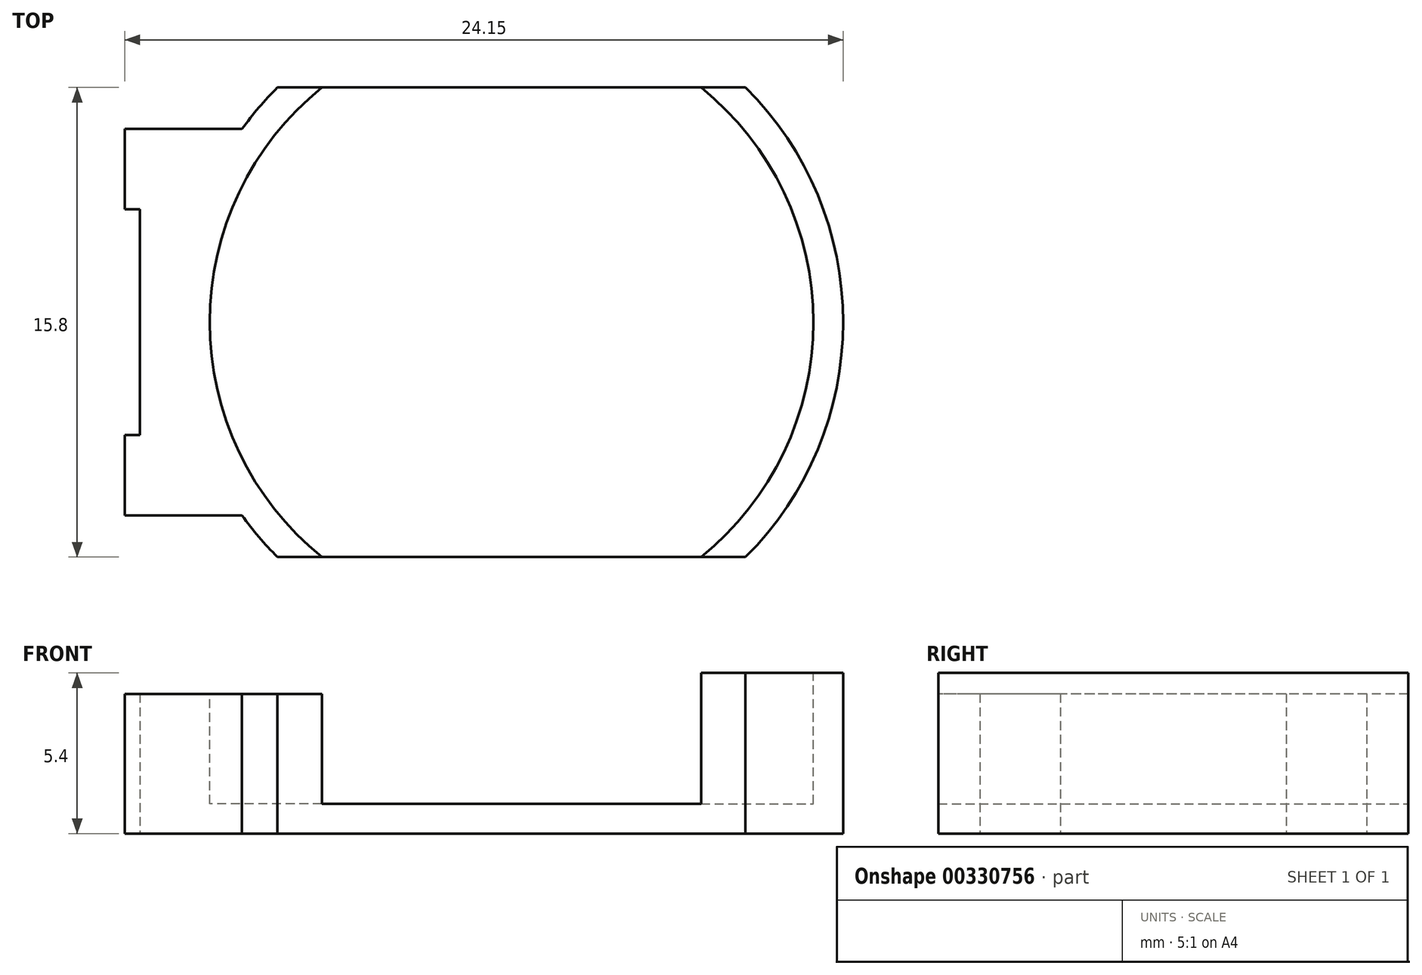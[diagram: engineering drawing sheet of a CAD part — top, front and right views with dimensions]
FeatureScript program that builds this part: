
annotation { "Feature Type Name" : "Feature", "Feature Type Description" : "" }
export const myFeature = defineFeature(function(context is Context, id is Id, definition is map)
    precondition{}
    {
        {
            var Q0;
            Q0=qCreatedBy(makeId("Top.planeOp"),FACE);
            var sketch = newSketch(context, id + "F0", { "sketchPlane" : qUnion([Q0])});
            skArc(sketch, "E0", {"start": v(-9.06, -6.5) * mm, "mid": v(-8.5, -7.22) * mm, "end": v(-7.87, -7.9) * mm});
            skLineSegment(sketch, "E1.bottom", {"start": v(-9.06, 6.5) * mm, "end": v(-13, 6.5) * mm});
            skLineSegment(sketch, "E1.top", {"start": v(-9.06, -6.5) * mm, "end": v(-13, -6.5) * mm});
            skLineSegment(sketch, "E1.right", {"start": v(-13, 6.5) * mm, "end": v(-13, 3.8) * mm});
            skLineSegment(sketch, "E2", {"start": v(-7.87, 7.9) * mm, "end": v(7.87, 7.9) * mm});
            skLineSegment(sketch, "E3", {"start": v(-7.87, -7.9) * mm, "end": v(7.87, -7.9) * mm});
            skArc(sketch, "E4.trimOffspring", {"start": v(-7.87, 7.9) * mm, "mid": v(-8.5, 7.22) * mm, "end": v(-9.06, 6.5) * mm});
            skArc(sketch, "E5.trimOffspring", {"start": v(7.87, -7.9) * mm, "mid": v(11.15, 0) * mm, "end": v(7.87, 7.9) * mm});
            skLineSegment(sketch, "E6.bottom", {"start": v(-13, 3.8) * mm, "end": v(-12.5, 3.8) * mm});
            skLineSegment(sketch, "E6.top", {"start": v(-13, -3.8) * mm, "end": v(-12.5, -3.8) * mm});
            skLineSegment(sketch, "E6.right", {"start": v(-12.5, 3.8) * mm, "end": v(-12.5, -3.8) * mm});
            skLineSegment(sketch, "E7.trimOffspring", {"start": v(-13, -3.8) * mm, "end": v(-13, -6.5) * mm});
            skSolve(sketch);
        }
        {
            var Q0;
            Q0=makeQuery(id+"F0.imprint","IMPRINT",FACE,{"disambiguationData":[TD([[makeQuery(id+"F0.imprint","IMPRINT",EDGE,{"derivedFrom":sQuery(id+"F0.wireOp",EDGE,"E0")}),1.0]])]});
            extrude(context, id + "F1", {"entities" : qUnion([Q0]), "depth" : 5.4 * mm});
        }
        {
            var Q0;
            Q0=makeQuery(id+"F1.opExtrude","CAP_FACE",FACE,{"disambiguationData":[OSD([sQuery(id+"F0.wireOp",EDGE,"E0"),sQuery(id+"F0.wireOp",EDGE,"E1.bottom"),sQuery(id+"F0.wireOp",EDGE,"E1.top"),sQuery(id+"F0.wireOp",EDGE,"E1.right"),sQuery(id+"F0.wireOp",EDGE,"E2"),sQuery(id+"F0.wireOp",EDGE,"E3"),sQuery(id+"F0.wireOp",EDGE,"E4.trimOffspring"),sQuery(id+"F0.wireOp",EDGE,"E5.trimOffspring"),sQuery(id+"F0.wireOp",EDGE,"E6.bottom"),sQuery(id+"F0.wireOp",EDGE,"E6.top"),sQuery(id+"F0.wireOp",EDGE,"E6.right"),sQuery(id+"F0.wireOp",EDGE,"E7.trimOffspring")])],"isStart":false});
            var sketch = newSketch(context, id + "F2", { "sketchPlane" : qUnion([Q0])});
            skCircle(sketch, "E8", {"center": v(0, 0) * mm, "radius": 10.15 * mm});
            skSolve(sketch);
        }
        {
            var Q0;
            {var subQ0=sQuery(id+"F2.wireOp",EDGE,"E8");var subQ1=makeQuery(id+"F1.opExtrude","CAP_EDGE",EDGE,{"disambiguationData":[OSD([sQuery(id+"F0.wireOp",EDGE,"E2")])],"isStart":false});var subQ2=makeQuery(id+"F2.imprint","INTERSECT",VERTEX,{"disambiguationData":[OD(0.0)],"derivedFrom":[subQ1,subQ0]});Q0=makeQuery(id+"F2.imprint","IMPRINT",FACE,{"disambiguationData":[TD([[makeQuery(id+"F2.imprint","IMPRINT",EDGE,{"disambiguationData":[TD([[subQ2,-1.0]])],"derivedFrom":subQ0}),1.0]])]});}
            extrude(context, id + "F3", {"entities" : qUnion([Q0]), "operationType" : NewBodyOperationType.REMOVE, "oppositeDirection" : true, "depth" : (5.4 - 1) * mm});
        }
        {
            var Q0;
            {var subQ0=sQuery(id+"F0.wireOp",EDGE,"E6.right");var subQ1=sQuery(id+"F0.wireOp",EDGE,"E6.bottom");var subQ2=sQuery(id+"F0.wireOp",EDGE,"E4.trimOffspring");var subQ3=sQuery(id+"F0.wireOp",EDGE,"E3");var subQ4=sQuery(id+"F0.wireOp",EDGE,"E2");var subQ5=sQuery(id+"F0.wireOp",EDGE,"E6.top");var subQ6=sQuery(id+"F0.wireOp",EDGE,"E0");var subQ7=sQuery(id+"F0.wireOp",EDGE,"E1.right");var subQ8=sQuery(id+"F0.wireOp",EDGE,"E1.bottom");var subQ9=sQuery(id+"F0.wireOp",EDGE,"E1.top");var subQ11=sQuery(id+"F0.wireOp",EDGE,"E7.trimOffspring");Q0=makeQuery(id+"F3.boolean.opBoolean","SPLIT",FACE,{"disambiguationData":[TD([makeQuery(id+"F1.opExtrude","SWEPT_FACE",FACE,{"disambiguationData":[OSD([subQ6])]})])],"derivedFrom":makeQuery(id+"F1.opExtrude","CAP_FACE",FACE,{"disambiguationData":[OSD([subQ6,subQ8,subQ9,subQ7,subQ4,subQ3,subQ2,sQuery(id+"F0.wireOp",EDGE,"E5.trimOffspring"),subQ1,subQ5,subQ0,subQ11])],"isStart":false})});}
            extrude(context, id + "F4", {"entities" : qUnion([Q0]), "operationType" : NewBodyOperationType.REMOVE, "oppositeDirection" : true, "depth" : (5.4 - 4.7) * mm});
        }
    });
